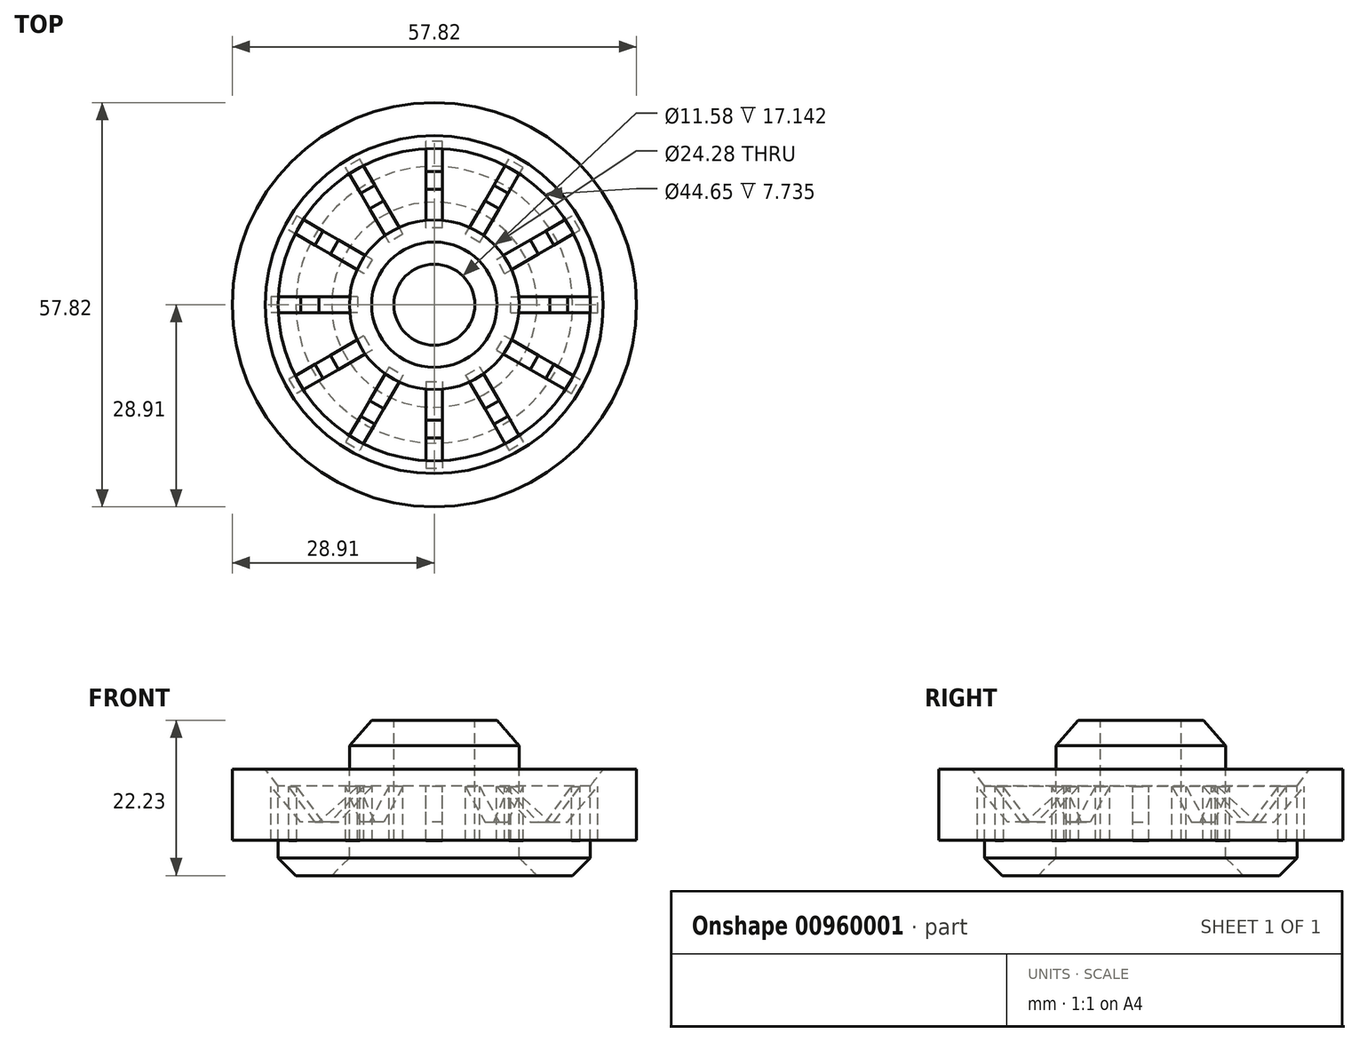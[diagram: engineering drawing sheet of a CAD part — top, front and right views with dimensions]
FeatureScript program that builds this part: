
annotation { "Feature Type Name" : "Feature", "Feature Type Description" : "" }
export const myFeature = defineFeature(function(context is Context, id is Id, definition is map)
    precondition{}
    {
        {
            var Q0;
            Q0=qCreatedBy(makeId("Front.planeOp"),FACE);
            var sketch = newSketch(context, id + "F0", { "sketchPlane" : qUnion([Q0])});
            skLineSegment(sketch, "E0", {"start": v(0, 0) * mm, "end": v(28.9, 0) * mm, "construction": true});
            skLineSegment(sketch, "E1", {"start": v(0, 0) * mm, "end": v(5.8, 0) * mm, "construction": true});
            skLineSegment(sketch, "E2.bottom", {"start": v(5.8, 0) * mm, "end": v(12.14, 0) * mm});
            skLineSegment(sketch, "E2.top", {"start": v(5.8, 22.23) * mm, "end": v(8.97, 22.23) * mm});
            skLineSegment(sketch, "E2.left", {"start": v(5.8, 0) * mm, "end": v(5.8, 22.23) * mm});
            skLineSegment(sketch, "E2.right", {"start": v(12.14, 0) * mm, "end": v(12.14, 18.57) * mm});
            skLineSegment(sketch, "E3", {"start": v(12.14, 0) * mm, "end": v(22.33, 0) * mm, "construction": true});
            skLineSegment(sketch, "E4.bottom", {"start": v(22.33, 0) * mm, "end": v(28.9, 0) * mm});
            skLineSegment(sketch, "E4.top", {"start": v(24.16, 15.24) * mm, "end": v(28.9, 15.24) * mm});
            skLineSegment(sketch, "E4.left", {"start": v(22.33, 0) * mm, "end": v(22.33, 12.82) * mm});
            skLineSegment(sketch, "E4.right", {"start": v(28.9, 0) * mm, "end": v(28.9, 15.24) * mm});
            skLineSegment(sketch, "E5.bottom", {"start": v(5.8, 0) * mm, "end": v(28.9, 0) * mm});
            skLineSegment(sketch, "E5.top", {"start": v(5.8, 5.08) * mm, "end": v(28.9, 5.08) * mm});
            skLineSegment(sketch, "E5.left", {"start": v(5.8, 0) * mm, "end": v(5.8, 5.08) * mm});
            skLineSegment(sketch, "E5.right", {"start": v(28.9, 0) * mm, "end": v(28.9, 5.08) * mm});
            skLineSegment(sketch, "E6", {"start": v(22.33, 12.82) * mm, "end": v(24.16, 15.24) * mm});
            skLineSegment(sketch, "E7", {"start": v(8.97, 22.23) * mm, "end": v(12.14, 18.57) * mm});
            skPoint(sketch, "E8.orphan", {"position": v(12.14, 22.23) * mm});
            skLineSegment(sketch, "E9", {"start": v(0, 59.7) * mm, "end": v(0, -35.87) * mm, "construction": true});
            skSolve(sketch);
        }
        {
            var Q0;
            Q0=makeQuery(id+"F0.imprint","IMPRINT",FACE,{"disambiguationData":[TD([[makeQuery(id+"F0.imprint","IMPRINT",EDGE,{"derivedFrom":sQuery(id+"F0.wireOp",EDGE,"E2.top")}),-1.0]])]});
            var Q1;
            {var subQ5=sQuery(id+"F0.wireOp",EDGE,"E5.left");Q1=makeQuery(id+"F0.imprint","IMPRINT",FACE,{"disambiguationData":[TD([[makeQuery(id+"F0.imprint","IMPRINT",EDGE,{"derivedFrom":subQ5}),-1.0]])]});}
            var Q2;
            {var subQ0=sQuery(id+"F0.wireOp",EDGE,"E5.bottom");var subQ1=sQuery(id+"F0.wireOp",EDGE,"E2.right");var subQ2=makeQuery(id+"F0.imprint","INTERSECT",VERTEX,{"derivedFrom":[subQ1,subQ0]});Q2=makeQuery(id+"F0.imprint","IMPRINT",FACE,{"disambiguationData":[TD([[makeQuery(id+"F0.imprint","IMPRINT",EDGE,{"disambiguationData":[TD([[subQ2,-1.0]])],"derivedFrom":subQ1}),-1.0]])]});}
            var Q3;
            {var subQ5=sQuery(id+"F0.wireOp",EDGE,"E5.right");Q3=makeQuery(id+"F0.imprint","IMPRINT",FACE,{"disambiguationData":[TD([[makeQuery(id+"F0.imprint","IMPRINT",EDGE,{"derivedFrom":subQ5}),1.0]])]});}
            var Q4;
            Q4=makeQuery(id+"F0.imprint","IMPRINT",FACE,{"disambiguationData":[TD([[makeQuery(id+"F0.imprint","IMPRINT",EDGE,{"derivedFrom":sQuery(id+"F0.wireOp",EDGE,"E4.top")}),-1.0]])]});
            var Q5;
            Q5=sQuery(id+"F0.wireOp",EDGE,"E9");
            revolve(context, id + "F1", {"surfaceOperationType" : NewSurfaceOperationType.NEW, "entities" : qUnion([Q0, Q1, Q2, Q3, Q4]), "axis" : qUnion([Q5]), "revolveType" : RevolveType.FULL});
        }
        {
            var Q0;
            Q0=makeQuery(id+"F1.opRevolve","SWEPT_EDGE",EDGE,{"disambiguationData":[OSD([sQuery(id+"F0.wireOp",EDGE,"E5.bottom"),sQuery(id+"F0.wireOp",EDGE,"E5.right")])]});
            chamfer(context, id + "F2", {"entities" : qUnion([Q0]), "width" : 2.54 * mm, "tangentPropagation" : true});
        }
        {
            var Q0;
            Q0=qCreatedBy(makeId("Front.planeOp"),FACE);
            var sketch = newSketch(context, id + "F3", { "sketchPlane" : qUnion([Q0])});
            skLineSegment(sketch, "E10.bottom", {"start": v(10.96, 4.99) * mm, "end": v(23.36, 4.99) * mm});
            skLineSegment(sketch, "E10.top", {"start": v(10.96, 12.73) * mm, "end": v(23.36, 12.73) * mm});
            skLineSegment(sketch, "E10.left", {"start": v(10.96, 4.99) * mm, "end": v(10.96, 12.73) * mm});
            skLineSegment(sketch, "E10.right", {"start": v(23.36, 4.99) * mm, "end": v(23.36, 12.73) * mm});
            skLineSegment(sketch, "E11", {"start": v(10.96, 12.73) * mm, "end": v(17.95, 6.32) * mm});
            skLineSegment(sketch, "E12", {"start": v(17.95, 6.32) * mm, "end": v(23.36, 12.73) * mm});
            skLineSegment(sketch, "E13.top", {"start": v(10.96, 7.65) * mm, "end": v(23.36, 7.65) * mm});
            skLineSegment(sketch, "E13.left", {"start": v(10.96, 4.99) * mm, "end": v(10.96, 7.65) * mm});
            skLineSegment(sketch, "E13.right", {"start": v(23.36, 4.99) * mm, "end": v(23.36, 7.65) * mm});
            skSolve(sketch);
        }
        {
            var Q0;
            {var subQ0=sQuery(id+"F3.wireOp",EDGE,"E10.left");Q0=makeQuery(id+"F3.imprint","IMPRINT",FACE,{"disambiguationData":[TD([[makeQuery(id+"F3.imprint","IMPRINT",EDGE,{"derivedFrom":subQ0}),-1.0]])]});}
            var Q1;
            Q1=makeQuery(id+"F3.imprint","IMPRINT",FACE,{"disambiguationData":[TD([[makeQuery(id+"F3.imprint","IMPRINT",EDGE,{"derivedFrom":sQuery(id+"F3.wireOp",EDGE,"E10.bottom")}),1.0]])]});
            var Q2;
            {var subQ0=sQuery(id+"F3.wireOp",EDGE,"E10.right");Q2=makeQuery(id+"F3.imprint","IMPRINT",FACE,{"disambiguationData":[TD([[makeQuery(id+"F3.imprint","IMPRINT",EDGE,{"derivedFrom":subQ0}),1.0]])]});}
            var Q3;
            {var subQ0=sQuery(id+"F3.wireOp",EDGE,"E12");var subQ1=sQuery(id+"F3.wireOp",EDGE,"E11");var subQ2=makeQuery(id+"F3.imprint","INTERSECT",VERTEX,{"derivedFrom":[subQ1,subQ0]});Q3=makeQuery(id+"F3.imprint","IMPRINT",FACE,{"disambiguationData":[TD([[makeQuery(id+"F3.imprint","IMPRINT",EDGE,{"disambiguationData":[TD([[subQ2,1.0]])],"derivedFrom":subQ1}),1.0]])]});}
            extrude(context, id + "F4", {"entities" : qUnion([Q0, Q1, Q2, Q3]), "endBound" : BoundingType.SYMMETRIC, "depth" : 2.34 * mm, "offsetDistance" : 25.4 * mm});
        }
        {
            var Q0;
            Q0=qCreatedBy(makeId("Front.planeOp"),FACE);
            var sketch = newSketch(context, id + "F5", { "sketchPlane" : qUnion([Q0])});
            skLineSegment(sketch, "E14", {"start": v(0, 44.6) * mm, "end": v(0, -15.9) * mm, "construction": true});
            skSolve(sketch);
        }
        {
            var Q0;
            Q0=makeQuery(id+"F4.opExtrude","SWEPT_BODY",BODY,{"disambiguationData":[OSD([sQuery(id+"F3.wireOp",EDGE,"E10.left"),sQuery(id+"F3.wireOp",EDGE,"E10.right"),sQuery(id+"F3.wireOp",EDGE,"E11"),sQuery(id+"F3.wireOp",EDGE,"E12"),sQuery(id+"F3.wireOp",EDGE,"E10.bottom"),sQuery(id+"F3.wireOp",EDGE,"E13.top"),sQuery(id+"F3.wireOp",EDGE,"E13.left"),sQuery(id+"F3.wireOp",EDGE,"E13.right")])]});
            var Q1;
            Q1=sQuery(id+"F5.wireOp",EDGE,"E14");
            circularPattern(context, id + "F6", {"entities" : qUnion([Q0]), "axis" : qUnion([Q1]), "angle" : 360 * degree, "instanceCount" : 12, "equalSpace" : true});
        }
        {
            var Q0;
            Q0=qCreatedBy(makeId("Top.planeOp"),FACE);
            var sketch = newSketch(context, id + "F7", { "sketchPlane" : qUnion([Q0])});
            skLineSegment(sketch, "E15", {"start": v(0, 0) * mm, "end": v(0, 7.11) * mm, "construction": true});
            skCircle(sketch, "E16.cCircle", {"center": v(0, 0) * mm, "radius": 7.11 * mm, "construction": true});
            skLineSegment(sketch, "E16.0", {"start": v(-4.1, 7.11) * mm, "end": v(4.1, 7.11) * mm});
            skLineSegment(sketch, "E16.1", {"start": v(4.1, 7.11) * mm, "end": v(8.21, 0) * mm});
            skLineSegment(sketch, "E16.2", {"start": v(8.21, 0) * mm, "end": v(4.1, -7.11) * mm});
            skLineSegment(sketch, "E16.3", {"start": v(4.1, -7.11) * mm, "end": v(-4.1, -7.11) * mm});
            skLineSegment(sketch, "E16.4", {"start": v(-4.1, -7.11) * mm, "end": v(-8.21, 0) * mm});
            skLineSegment(sketch, "E16.5", {"start": v(-8.21, 0) * mm, "end": v(-4.1, 7.11) * mm});
            skPoint(sketch, "E16.0.midPoint", {"position": v(0, 7.11) * mm});
            skSolve(sketch);
        }
        {
            var Q0;
            Q0=makeQuery(id+"F7.imprint","IMPRINT",FACE,{"disambiguationData":[TD([[makeQuery(id+"F7.imprint","IMPRINT",EDGE,{"derivedFrom":sQuery(id+"F7.wireOp",EDGE,"E16.0")}),-1.0]])]});
            extrude(context, id + "F8", {"entities" : qUnion([Q0]), "depth" : 8.23 * mm, "offsetDistance" : 25.4 * mm});
        }
        {
            var Q0;
            Q0=makeQuery(id+"F8.opExtrude","SWEPT_BODY",BODY,{"disambiguationData":[OSD([sQuery(id+"F7.wireOp",EDGE,"E16.0"),sQuery(id+"F7.wireOp",EDGE,"E16.1"),sQuery(id+"F7.wireOp",EDGE,"E16.2"),sQuery(id+"F7.wireOp",EDGE,"E16.3"),sQuery(id+"F7.wireOp",EDGE,"E16.4"),sQuery(id+"F7.wireOp",EDGE,"E16.5")])]});
            transform(context, id + "F9", {"entities" : qUnion([Q0]), "transformType" : TransformType.TRANSLATION_3D, "dx" : 0 * mm, "dy" : 0 * mm, "dz" : 8.2 * mm, "makeCopy" : false});
        }
        {
            var Q0;
            Q0=makeQuery(id+"F8.opExtrude","SWEPT_BODY",BODY,{"disambiguationData":[OSD([sQuery(id+"F7.wireOp",EDGE,"E16.0"),sQuery(id+"F7.wireOp",EDGE,"E16.1"),sQuery(id+"F7.wireOp",EDGE,"E16.2"),sQuery(id+"F7.wireOp",EDGE,"E16.3"),sQuery(id+"F7.wireOp",EDGE,"E16.4"),sQuery(id+"F7.wireOp",EDGE,"E16.5")])]});
            var Q1;
            Q1=makeQuery(id+"F6.opPattern","COPY",BODY,{"derivedFrom":makeQuery(id+"F4.opExtrude","SWEPT_BODY",BODY,{"disambiguationData":[OSD([sQuery(id+"F3.wireOp",EDGE,"E10.left"),sQuery(id+"F3.wireOp",EDGE,"E10.right"),sQuery(id+"F3.wireOp",EDGE,"E11"),sQuery(id+"F3.wireOp",EDGE,"E12"),sQuery(id+"F3.wireOp",EDGE,"E10.bottom"),sQuery(id+"F3.wireOp",EDGE,"E13.top"),sQuery(id+"F3.wireOp",EDGE,"E13.left"),sQuery(id+"F3.wireOp",EDGE,"E13.right")])]}),"instanceName":"4"});
            booleanBodies(context, id + "F10", {"operationType" : BooleanOperationType.SUBTRACTION, "tools" : qUnion([Q0]), "targets" : qUnion([Q1])});
        }
        {
            var Q0;
            Q0=qCreatedBy(makeId("Top.planeOp"),FACE);
            var sketch = newSketch(context, id + "F11", { "sketchPlane" : qUnion([Q0])});
            skCircle(sketch, "E17", {"center": v(0, 28.86) * mm, "radius": 2.03 * mm});
            skSolve(sketch);
        }
        {
            var Q0;
            Q0=qCreatedBy(makeId("Front.planeOp"),FACE);
            var sketch = newSketch(context, id + "F12", { "sketchPlane" : qUnion([Q0])});
            skLineSegment(sketch, "E18", {"start": v(0, 45.1) * mm, "end": v(0, -21.98) * mm, "construction": true});
            skSolve(sketch);
        }
        {
            var Q0;
            Q0=makeQuery(id+"F11.imprint","IMPRINT",FACE,{"disambiguationData":[TD([[makeQuery(id+"F11.imprint","IMPRINT",EDGE,{"derivedFrom":sQuery(id+"F11.wireOp",EDGE,"E17")}),1.0]])]});
            var Q1;
            Q1=sQuery(id+"F11.wireOp",EDGE,"E17");
            extrude(context, id + "F13", {"entities" : qUnion([Q0]), "surfaceEntities" : qUnion([Q1]), "depth" : 25.4 * mm, "offsetDistance" : 25.4 * mm});
        }
        {
            var Q0;
            Q0=makeQuery(id+"F13.opExtrude","SWEPT_BODY",BODY,{"disambiguationData":[OSD([sQuery(id+"F11.wireOp",EDGE,"E17")])]});
            var Q1;
            Q1=sQuery(id+"F12.wireOp",EDGE,"E18");
            circularPattern(context, id + "F14", {"entities" : qUnion([Q0]), "axis" : qUnion([Q1]), "angle" : 360 * degree, "instanceCount" : 28, "equalSpace" : true});
        }
        {
            var Q0;
            Q0=makeQuery(id+"F14.opPattern","COPY",BODY,{"derivedFrom":makeQuery(id+"F13.opExtrude","SWEPT_BODY",BODY,{"disambiguationData":[OSD([sQuery(id+"F11.wireOp",EDGE,"E17")])]}),"instanceName":"4"});
            var Q1;
            Q1=makeQuery(id+"F13.opExtrude","SWEPT_BODY",BODY,{"disambiguationData":[OSD([sQuery(id+"F11.wireOp",EDGE,"E17")])]});
            var Q2;
            Q2=makeQuery(id+"F14.opPattern","COPY",BODY,{"derivedFrom":makeQuery(id+"F13.opExtrude","SWEPT_BODY",BODY,{"disambiguationData":[OSD([sQuery(id+"F11.wireOp",EDGE,"E17")])]}),"instanceName":"3"});
            var Q3;
            Q3=makeQuery(id+"F14.opPattern","COPY",BODY,{"derivedFrom":makeQuery(id+"F13.opExtrude","SWEPT_BODY",BODY,{"disambiguationData":[OSD([sQuery(id+"F11.wireOp",EDGE,"E17")])]}),"instanceName":"6"});
            var Q4;
            Q4=makeQuery(id+"F14.opPattern","COPY",BODY,{"derivedFrom":makeQuery(id+"F13.opExtrude","SWEPT_BODY",BODY,{"disambiguationData":[OSD([sQuery(id+"F11.wireOp",EDGE,"E17")])]}),"instanceName":"8"});
            var Q5;
            Q5=makeQuery(id+"F14.opPattern","COPY",BODY,{"derivedFrom":makeQuery(id+"F13.opExtrude","SWEPT_BODY",BODY,{"disambiguationData":[OSD([sQuery(id+"F11.wireOp",EDGE,"E17")])]}),"instanceName":"7"});
            var Q6;
            Q6=makeQuery(id+"F14.opPattern","COPY",BODY,{"derivedFrom":makeQuery(id+"F13.opExtrude","SWEPT_BODY",BODY,{"disambiguationData":[OSD([sQuery(id+"F11.wireOp",EDGE,"E17")])]}),"instanceName":"5"});
            var Q7;
            Q7=makeQuery(id+"F14.opPattern","COPY",BODY,{"derivedFrom":makeQuery(id+"F13.opExtrude","SWEPT_BODY",BODY,{"disambiguationData":[OSD([sQuery(id+"F11.wireOp",EDGE,"E17")])]}),"instanceName":"2"});
            var Q8;
            Q8=makeQuery(id+"F14.opPattern","COPY",BODY,{"derivedFrom":makeQuery(id+"F13.opExtrude","SWEPT_BODY",BODY,{"disambiguationData":[OSD([sQuery(id+"F11.wireOp",EDGE,"E17")])]}),"instanceName":"1"});
            var Q9;
            Q9=makeQuery(id+"F14.opPattern","COPY",BODY,{"derivedFrom":makeQuery(id+"F13.opExtrude","SWEPT_BODY",BODY,{"disambiguationData":[OSD([sQuery(id+"F11.wireOp",EDGE,"E17")])]}),"instanceName":"9"});
            var Q10;
            Q10=makeQuery(id+"F14.opPattern","COPY",BODY,{"derivedFrom":makeQuery(id+"F13.opExtrude","SWEPT_BODY",BODY,{"disambiguationData":[OSD([sQuery(id+"F11.wireOp",EDGE,"E17")])]}),"instanceName":"10"});
            var Q11;
            Q11=makeQuery(id+"F14.opPattern","COPY",BODY,{"derivedFrom":makeQuery(id+"F13.opExtrude","SWEPT_BODY",BODY,{"disambiguationData":[OSD([sQuery(id+"F11.wireOp",EDGE,"E17")])]}),"instanceName":"11"});
            var Q12;
            Q12=makeQuery(id+"F14.opPattern","COPY",BODY,{"derivedFrom":makeQuery(id+"F13.opExtrude","SWEPT_BODY",BODY,{"disambiguationData":[OSD([sQuery(id+"F11.wireOp",EDGE,"E17")])]}),"instanceName":"12"});
            var Q13;
            Q13=makeQuery(id+"F14.opPattern","COPY",BODY,{"derivedFrom":makeQuery(id+"F13.opExtrude","SWEPT_BODY",BODY,{"disambiguationData":[OSD([sQuery(id+"F11.wireOp",EDGE,"E17")])]}),"instanceName":"13"});
            var Q14;
            Q14=makeQuery(id+"F14.opPattern","COPY",BODY,{"derivedFrom":makeQuery(id+"F13.opExtrude","SWEPT_BODY",BODY,{"disambiguationData":[OSD([sQuery(id+"F11.wireOp",EDGE,"E17")])]}),"instanceName":"14"});
            var Q15;
            Q15=makeQuery(id+"F14.opPattern","COPY",BODY,{"derivedFrom":makeQuery(id+"F13.opExtrude","SWEPT_BODY",BODY,{"disambiguationData":[OSD([sQuery(id+"F11.wireOp",EDGE,"E17")])]}),"instanceName":"15"});
            var Q16;
            Q16=makeQuery(id+"F14.opPattern","COPY",BODY,{"derivedFrom":makeQuery(id+"F13.opExtrude","SWEPT_BODY",BODY,{"disambiguationData":[OSD([sQuery(id+"F11.wireOp",EDGE,"E17")])]}),"instanceName":"16"});
            var Q17;
            Q17=makeQuery(id+"F14.opPattern","COPY",BODY,{"derivedFrom":makeQuery(id+"F13.opExtrude","SWEPT_BODY",BODY,{"disambiguationData":[OSD([sQuery(id+"F11.wireOp",EDGE,"E17")])]}),"instanceName":"17"});
            var Q18;
            Q18=makeQuery(id+"F14.opPattern","COPY",BODY,{"derivedFrom":makeQuery(id+"F13.opExtrude","SWEPT_BODY",BODY,{"disambiguationData":[OSD([sQuery(id+"F11.wireOp",EDGE,"E17")])]}),"instanceName":"18"});
            var Q19;
            Q19=makeQuery(id+"F14.opPattern","COPY",BODY,{"derivedFrom":makeQuery(id+"F13.opExtrude","SWEPT_BODY",BODY,{"disambiguationData":[OSD([sQuery(id+"F11.wireOp",EDGE,"E17")])]}),"instanceName":"19"});
            var Q20;
            Q20=makeQuery(id+"F14.opPattern","COPY",BODY,{"derivedFrom":makeQuery(id+"F13.opExtrude","SWEPT_BODY",BODY,{"disambiguationData":[OSD([sQuery(id+"F11.wireOp",EDGE,"E17")])]}),"instanceName":"20"});
            var Q21;
            Q21=makeQuery(id+"F14.opPattern","COPY",BODY,{"derivedFrom":makeQuery(id+"F13.opExtrude","SWEPT_BODY",BODY,{"disambiguationData":[OSD([sQuery(id+"F11.wireOp",EDGE,"E17")])]}),"instanceName":"21"});
            var Q22;
            Q22=makeQuery(id+"F14.opPattern","COPY",BODY,{"derivedFrom":makeQuery(id+"F13.opExtrude","SWEPT_BODY",BODY,{"disambiguationData":[OSD([sQuery(id+"F11.wireOp",EDGE,"E17")])]}),"instanceName":"22"});
            var Q23;
            Q23=makeQuery(id+"F14.opPattern","COPY",BODY,{"derivedFrom":makeQuery(id+"F13.opExtrude","SWEPT_BODY",BODY,{"disambiguationData":[OSD([sQuery(id+"F11.wireOp",EDGE,"E17")])]}),"instanceName":"23"});
            var Q24;
            Q24=makeQuery(id+"F14.opPattern","COPY",BODY,{"derivedFrom":makeQuery(id+"F13.opExtrude","SWEPT_BODY",BODY,{"disambiguationData":[OSD([sQuery(id+"F11.wireOp",EDGE,"E17")])]}),"instanceName":"24"});
            var Q25;
            Q25=makeQuery(id+"F14.opPattern","COPY",BODY,{"derivedFrom":makeQuery(id+"F13.opExtrude","SWEPT_BODY",BODY,{"disambiguationData":[OSD([sQuery(id+"F11.wireOp",EDGE,"E17")])]}),"instanceName":"25"});
            var Q26;
            Q26=makeQuery(id+"F14.opPattern","COPY",BODY,{"derivedFrom":makeQuery(id+"F13.opExtrude","SWEPT_BODY",BODY,{"disambiguationData":[OSD([sQuery(id+"F11.wireOp",EDGE,"E17")])]}),"instanceName":"26"});
            var Q27;
            Q27=makeQuery(id+"F14.opPattern","COPY",BODY,{"derivedFrom":makeQuery(id+"F13.opExtrude","SWEPT_BODY",BODY,{"disambiguationData":[OSD([sQuery(id+"F11.wireOp",EDGE,"E17")])]}),"instanceName":"27"});
            var Q28;
            Q28=makeQuery(id+"F6.opPattern","COPY",BODY,{"derivedFrom":makeQuery(id+"F4.opExtrude","SWEPT_BODY",BODY,{"disambiguationData":[OSD([sQuery(id+"F3.wireOp",EDGE,"E10.left"),sQuery(id+"F3.wireOp",EDGE,"E10.right"),sQuery(id+"F3.wireOp",EDGE,"E11"),sQuery(id+"F3.wireOp",EDGE,"E12"),sQuery(id+"F3.wireOp",EDGE,"E10.bottom"),sQuery(id+"F3.wireOp",EDGE,"E13.top"),sQuery(id+"F3.wireOp",EDGE,"E13.left"),sQuery(id+"F3.wireOp",EDGE,"E13.right")])]}),"instanceName":"4"});
            booleanBodies(context, id + "F15", {"operationType" : BooleanOperationType.SUBTRACTION, "tools" : qUnion([Q0, Q1, Q2, Q3, Q4, Q5, Q6, Q7, Q8, Q9, Q10, Q11, Q12, Q13, Q14, Q15, Q16, Q17, Q18, Q19, Q20, Q21, Q22, Q23, Q24, Q25, Q26, Q27]), "targets" : qUnion([Q28])});
        }
    });
